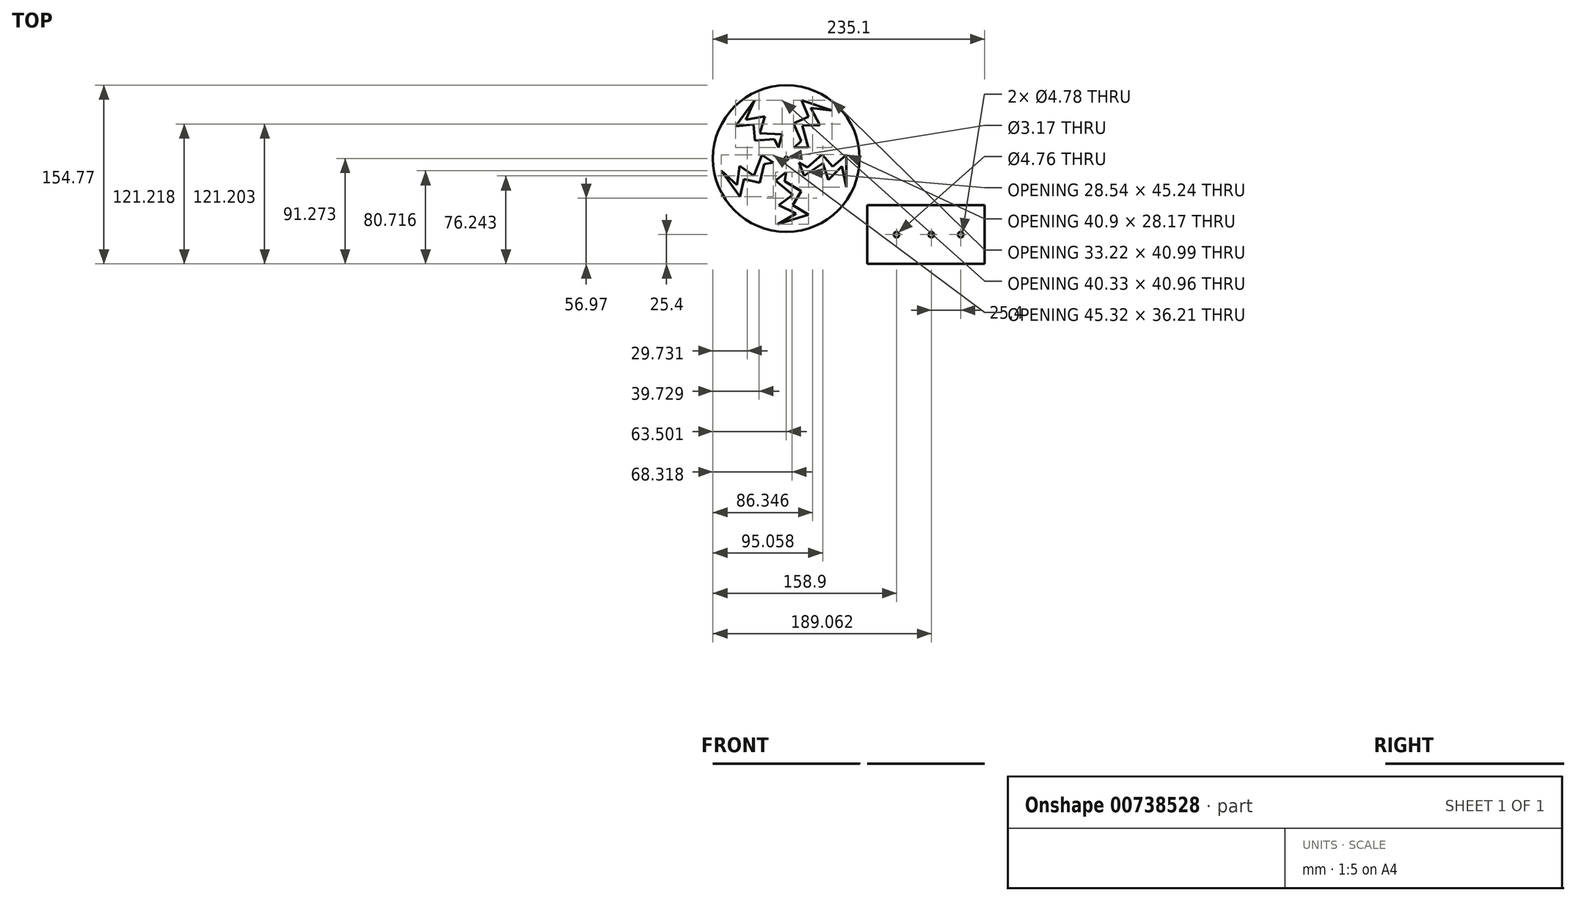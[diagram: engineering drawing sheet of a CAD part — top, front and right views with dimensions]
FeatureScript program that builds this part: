
annotation { "Feature Type Name" : "Feature", "Feature Type Description" : "" }
export const myFeature = defineFeature(function(context is Context, id is Id, definition is map)
    precondition{}
    {
        {
            var Q0;
            Q0=qCreatedBy(makeId("Top.planeOp"),FACE);
            var sketch = newSketch(context, id + "F0", { "sketchPlane" : qUnion([Q0])});
            skLineSegment(sketch, "E0.bottom", {"start": v(0, 0) * mm, "end": v(101.6, 0) * mm});
            skLineSegment(sketch, "E0.top", {"start": v(0, -50.8) * mm, "end": v(101.6, -50.8) * mm});
            skLineSegment(sketch, "E0.left", {"start": v(0, 0) * mm, "end": v(0, -50.8) * mm});
            skLineSegment(sketch, "E0.right", {"start": v(101.6, 0) * mm, "end": v(101.6, -50.8) * mm});
            skSolve(sketch);
        }
        {
            var Q0;
            Q0=makeQuery(id+"F0.imprint","IMPRINT",FACE,{"disambiguationData":[TD([[makeQuery(id+"F0.imprint","IMPRINT",EDGE,{"derivedFrom":sQuery(id+"F0.wireOp",EDGE,"E0.bottom")}),-1.0]])]});
            extrude(context, id + "F1", {"entities" : qUnion([Q0]), "depth" : 1 / 203.2 * mm, "offsetDistance" : 25.4 * mm});
        }
        {
            var Q0;
            Q0=makeQuery(id+"F1.opExtrude","CAP_FACE",FACE,{"disambiguationData":[OSD([sQuery(id+"F0.wireOp",EDGE,"E0.bottom"),sQuery(id+"F0.wireOp",EDGE,"E0.top"),sQuery(id+"F0.wireOp",EDGE,"E0.left"),sQuery(id+"F0.wireOp",EDGE,"E0.right")])],"isStart":false});
            var sketch = newSketch(context, id + "F2", { "sketchPlane" : qUnion([Q0])});
            skLineSegment(sketch, "E1", {"start": v(0, -25.4) * mm, "end": v(25.4, -25.4) * mm});
            skCircle(sketch, "E2", {"center": v(25.4, -25.4) * mm, "radius": 2.38 * mm});
            skLineSegment(sketch, "E3", {"start": v(25.4, -25.4) * mm, "end": v(55.56, -25.4) * mm});
            skCircle(sketch, "E4", {"center": v(55.56, -25.4) * mm, "radius": 2.39 * mm});
            skLineSegment(sketch, "E5", {"start": v(55.56, -25.4) * mm, "end": v(80.96, -25.4) * mm});
            skCircle(sketch, "E6", {"center": v(80.96, -25.4) * mm, "radius": 2.39 * mm});
            skSolve(sketch);
        }
        {
            var Q0;
            {var subQ0=sQuery(id+"F2.wireOp",EDGE,"E3");var subQ1=sQuery(id+"F2.wireOp",EDGE,"E1");var subQ2=makeQuery(id+"F2.imprint","INTERSECT",VERTEX,{"derivedFrom":[subQ1,subQ0]});Q0=makeQuery(id+"F2.imprint","IMPRINT",FACE,{"disambiguationData":[TD([[makeQuery(id+"F2.imprint","IMPRINT",EDGE,{"disambiguationData":[TD([[subQ2,1.0]])],"derivedFrom":subQ1}),1.0]])]});}
            var Q1;
            {var subQ0=sQuery(id+"F2.wireOp",EDGE,"E3");var subQ1=sQuery(id+"F2.wireOp",EDGE,"E1");var subQ2=makeQuery(id+"F2.imprint","INTERSECT",VERTEX,{"derivedFrom":[subQ1,subQ0]});Q1=makeQuery(id+"F2.imprint","IMPRINT",FACE,{"disambiguationData":[TD([[makeQuery(id+"F2.imprint","IMPRINT",EDGE,{"disambiguationData":[TD([[subQ2,1.0]])],"derivedFrom":subQ1}),-1.0]])]});}
            var Q2;
            {var subQ0=sQuery(id+"F2.wireOp",EDGE,"E5");var subQ1=sQuery(id+"F2.wireOp",EDGE,"E3");var subQ2=makeQuery(id+"F2.imprint","INTERSECT",VERTEX,{"derivedFrom":[subQ1,subQ0]});Q2=makeQuery(id+"F2.imprint","IMPRINT",FACE,{"disambiguationData":[TD([[makeQuery(id+"F2.imprint","IMPRINT",EDGE,{"disambiguationData":[TD([[subQ2,1.0]])],"derivedFrom":subQ1}),-1.0]])]});}
            var Q3;
            {var subQ0=sQuery(id+"F2.wireOp",EDGE,"E5");var subQ1=sQuery(id+"F2.wireOp",EDGE,"E3");var subQ2=makeQuery(id+"F2.imprint","INTERSECT",VERTEX,{"derivedFrom":[subQ1,subQ0]});Q3=makeQuery(id+"F2.imprint","IMPRINT",FACE,{"disambiguationData":[TD([[makeQuery(id+"F2.imprint","IMPRINT",EDGE,{"disambiguationData":[TD([[subQ2,1.0]])],"derivedFrom":subQ1}),1.0]])]});}
            var Q4;
            Q4=makeQuery(id+"F2.imprint","IMPRINT",FACE,{"disambiguationData":[TD([[makeQuery(id+"F2.imprint","IMPRINT",EDGE,{"derivedFrom":sQuery(id+"F2.wireOp",EDGE,"E6")}),1.0]])]});
            extrude(context, id + "F3", {"entities" : qUnion([Q0, Q1, Q2, Q3, Q4]), "operationType" : NewBodyOperationType.REMOVE, "endBound" : BoundingType.THROUGH_ALL, "oppositeDirection" : true, "depth" : 25.4 * mm, "offsetDistance" : 25.4 * mm});
        }
        {
            var Q0;
            Q0=makeQuery(id+"F1.opExtrude","SWEPT_FACE",FACE,{"disambiguationData":[OSD([sQuery(id+"F0.wireOp",EDGE,"E0.bottom")])]});
            var sketch = newSketch(context, id + "F4", { "sketchPlane" : qUnion([Q0])});
            skSolve(sketch);
        }
        {
            var Q0;
            Q0=qCreatedBy(makeId("Top.planeOp"),FACE);
            var sketch = newSketch(context, id + "F5", { "sketchPlane" : qUnion([Q0])});
            skCircle(sketch, "E7", {"center": v(-70, 40.47) * mm, "radius": 63.5 * mm});
            skCircle(sketch, "E8", {"center": v(-70, 40.47) * mm, "radius": 1.59 * mm});
            skLineSegment(sketch, "E9", {"start": v(-70, 28.8) * mm, "end": v(-79.45, 21.33) * mm});
            skLineSegment(sketch, "E10", {"start": v(-79.45, 21.33) * mm, "end": v(-64.3, 9.16) * mm});
            skLineSegment(sketch, "E11", {"start": v(-64.3, 9.16) * mm, "end": v(-76.37, 0) * mm});
            skLineSegment(sketch, "E12", {"start": v(-76.37, 0) * mm, "end": v(-61.43, -7.27) * mm});
            skLineSegment(sketch, "E13", {"start": v(-61.43, -7.27) * mm, "end": v(-77.41, -16.45) * mm});
            skLineSegment(sketch, "E14", {"start": v(-77.41, -16.45) * mm, "end": v(-50.91, -8) * mm});
            skLineSegment(sketch, "E15", {"start": v(-50.91, -8) * mm, "end": v(-64.28, 0) * mm});
            skLineSegment(sketch, "E16", {"start": v(-64.28, 0) * mm, "end": v(-57.06, 12.05) * mm});
            skLineSegment(sketch, "E17", {"start": v(-57.06, 12.05) * mm, "end": v(-71.47, 20.7) * mm});
            skLineSegment(sketch, "E18", {"start": v(-71.47, 20.7) * mm, "end": v(-70, 28.8) * mm});
            skLineSegment(sketch, "E19.1.0", {"start": v(-58.9, 36.86) * mm, "end": v(-54.71, 25.57) * mm});
            skLineSegment(sketch, "E19.1.1", {"start": v(-51.64, 32.96) * mm, "end": v(-58.9, 36.86) * mm});
            skLineSegment(sketch, "E19.1.2", {"start": v(-38.97, 44) * mm, "end": v(-51.64, 32.96) * mm});
            skLineSegment(sketch, "E19.1.3", {"start": v(-29.74, 33.4) * mm, "end": v(-38.97, 44) * mm});
            skLineSegment(sketch, "E19.1.4", {"start": v(-18, 43.64) * mm, "end": v(-29.74, 33.4) * mm});
            skLineSegment(sketch, "E19.1.5", {"start": v(-18.15, 15.83) * mm, "end": v(-18, 43.64) * mm});
            skLineSegment(sketch, "E19.1.6", {"start": v(-21.95, 33.87) * mm, "end": v(-18.15, 15.83) * mm});
            skLineSegment(sketch, "E19.1.7", {"start": v(-33.48, 21.9) * mm, "end": v(-21.95, 33.87) * mm});
            skLineSegment(sketch, "E19.1.8", {"start": v(-38.46, 36.21) * mm, "end": v(-33.48, 21.9) * mm});
            skLineSegment(sketch, "E19.1.9", {"start": v(-54.71, 25.57) * mm, "end": v(-38.46, 36.21) * mm});
            skLineSegment(sketch, "E19.2.0", {"start": v(-63.13, 49.92) * mm, "end": v(-51.1, 50.4) * mm});
            skLineSegment(sketch, "E19.2.1", {"start": v(-57.18, 55.6) * mm, "end": v(-63.13, 49.92) * mm});
            skLineSegment(sketch, "E19.2.2", {"start": v(-63.77, 71.07) * mm, "end": v(-57.18, 55.6) * mm});
            skLineSegment(sketch, "E19.2.3", {"start": v(-50.84, 76.58) * mm, "end": v(-63.77, 71.07) * mm});
            skLineSegment(sketch, "E19.2.4", {"start": v(-56.94, 90.91) * mm, "end": v(-50.84, 76.58) * mm});
            skLineSegment(sketch, "E19.2.5", {"start": v(-30.54, 82.17) * mm, "end": v(-56.94, 90.91) * mm});
            skLineSegment(sketch, "E19.2.6", {"start": v(-48.87, 84.13) * mm, "end": v(-30.54, 82.17) * mm});
            skLineSegment(sketch, "E19.2.7", {"start": v(-41.06, 69.47) * mm, "end": v(-48.87, 84.13) * mm});
            skLineSegment(sketch, "E19.2.8", {"start": v(-56.2, 69.16) * mm, "end": v(-41.06, 69.47) * mm});
            skLineSegment(sketch, "E19.2.9", {"start": v(-51.1, 50.4) * mm, "end": v(-56.2, 69.16) * mm});
            skLineSegment(sketch, "E19.3.0", {"start": v(-76.86, 49.92) * mm, "end": v(-73.6, 61.52) * mm});
            skLineSegment(sketch, "E19.3.1", {"start": v(-80.43, 57.34) * mm, "end": v(-76.86, 49.92) * mm});
            skLineSegment(sketch, "E19.3.2", {"start": v(-97.18, 55.86) * mm, "end": v(-80.43, 57.34) * mm});
            skLineSegment(sketch, "E19.3.3", {"start": v(-98.42, 69.85) * mm, "end": v(-97.18, 55.86) * mm});
            skLineSegment(sketch, "E19.3.4", {"start": v(-113.94, 68.48) * mm, "end": v(-98.42, 69.85) * mm});
            skLineSegment(sketch, "E19.3.5", {"start": v(-97.46, 90.88) * mm, "end": v(-113.94, 68.48) * mm});
            skLineSegment(sketch, "E19.3.6", {"start": v(-105, 74.06) * mm, "end": v(-97.46, 90.88) * mm});
            skLineSegment(sketch, "E19.3.7", {"start": v(-88.63, 76.96) * mm, "end": v(-105, 74.06) * mm});
            skLineSegment(sketch, "E19.3.8", {"start": v(-93.01, 62.46) * mm, "end": v(-88.63, 76.96) * mm});
            skLineSegment(sketch, "E19.3.9", {"start": v(-73.6, 61.52) * mm, "end": v(-93.01, 62.46) * mm});
            skLineSegment(sketch, "E19.4.0", {"start": v(-81.1, 36.86) * mm, "end": v(-91.13, 43.55) * mm});
            skLineSegment(sketch, "E19.4.1", {"start": v(-89.27, 35.76) * mm, "end": v(-81.1, 36.86) * mm});
            skLineSegment(sketch, "E19.4.2", {"start": v(-93.03, 19.38) * mm, "end": v(-89.27, 35.76) * mm});
            skLineSegment(sketch, "E19.4.3", {"start": v(-106.72, 22.52) * mm, "end": v(-93.03, 19.38) * mm});
            skLineSegment(sketch, "E19.4.4", {"start": v(-110.2, 7.34) * mm, "end": v(-106.72, 22.52) * mm});
            skLineSegment(sketch, "E19.4.5", {"start": v(-126.43, 29.93) * mm, "end": v(-110.2, 7.34) * mm});
            skLineSegment(sketch, "E19.4.6", {"start": v(-112.75, 17.57) * mm, "end": v(-126.43, 29.93) * mm});
            skLineSegment(sketch, "E19.4.7", {"start": v(-110.46, 34.03) * mm, "end": v(-112.75, 17.57) * mm});
            skLineSegment(sketch, "E19.4.8", {"start": v(-98.02, 25.38) * mm, "end": v(-110.46, 34.03) * mm});
            skLineSegment(sketch, "E19.4.9", {"start": v(-91.13, 43.55) * mm, "end": v(-98.02, 25.38) * mm});
            skSolve(sketch);
        }
        {
            var Q0;
            Q0=makeQuery(id+"F5.imprint","IMPRINT",FACE,{"disambiguationData":[TD([[makeQuery(id+"F5.imprint","IMPRINT",EDGE,{"derivedFrom":sQuery(id+"F5.wireOp",EDGE,"E7")}),1.0]])]});
            extrude(context, id + "F6", {"entities" : qUnion([Q0]), "depth" : 1 / 203.2 * mm, "offsetDistance" : 25.4 * mm});
        }
    });
